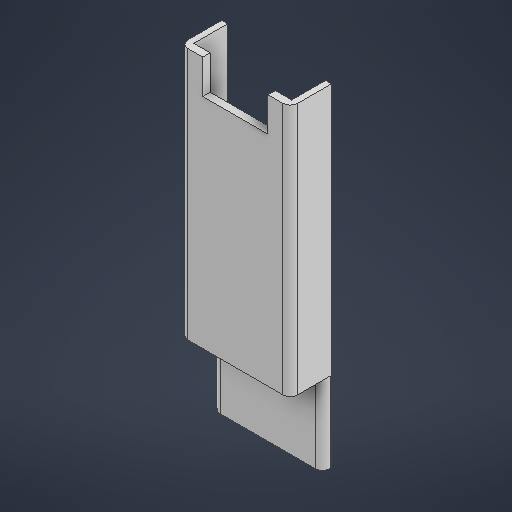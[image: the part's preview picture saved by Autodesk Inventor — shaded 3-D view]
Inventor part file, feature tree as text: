
AUTODESK INVENTOR PART (.ipt)
format: ipt  version: 2025 (Build 290162000, 162)  size: 278,528 bytes
history: native  units: in
note: dims shown in document units (in); Inventor stores cm internally (conversion verified against a paired STEP export)
features: sketch x6, extrude x5, chamfer x1, fillet x1
ambient origin geometry x8: Origin, YZ Plane, XZ Plane, XY Plane, X Axis, Y Axis, Z Axis, Center Point
bodies: Solid1 (feature_tree)
feature tree (13):
  extrude  "Extrusion1"  Depth=6.6929in
  extrude  "Extrusion2"  Depth=0.1969in
  extrude  "Extrusion3"  Depth=0.1575in TaperAngle=0.0deg
  extrude  "Extrusion4"  Depth=1.7323in
  chamfer  "Chamfer1"  Distance=0.8989in
  extrude  "Extrusion5"  Depth=0.2362in
  fillet  "Fillet1"  Radius=2.126in
  sketch  "Sketch1"  dims[d0=2.9134in d1=6.6929in]
  sketch  "Sketch2"  dims[d5=2.0472in d6=0.1575in d7=0.0in]
  sketch  "Sketch3"  dims[d8=0.1575in d9=1.7323in]
  sketch  "Sketch4"  dims[d10=0.9055in]
  sketch  "Sketch5"  dims[d12=0.1575in d13=0.8989in d14=0.0in d15=0.2362in d16=2.126in d17=0.0in d18=2.056in d19=0.2165in d20=0.2165in d21=2.9134in d23=4.3504in d24=90.0deg d25=0.1969in d26=0.5906in d27=1.9685in d29=0.7874in d30=0.3937in d32=0.3937in d34=0.1969in d35=0.0in d36=0.3937in d37=0.0787in d38=0.1632in d39=0.2028in d40=0.0197in d41=0.1969in]
  sketch  "Sketch Rectangular Pattern1"  dims[d2=0.1969in d3=0.0in d4=0.1969in]
